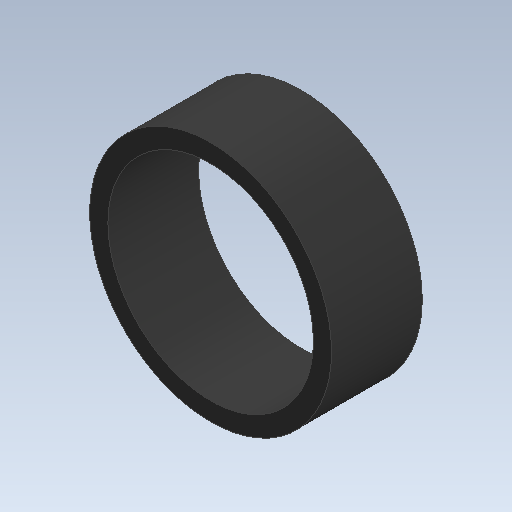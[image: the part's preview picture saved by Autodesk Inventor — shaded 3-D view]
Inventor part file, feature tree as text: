
AUTODESK INVENTOR PART (.ipt)
format: ipt  version: 2020 (Build 240168000, 168)  size: 94,208 bytes
history: native  units: in
note: dims shown in document units (in); Inventor stores cm internally (conversion verified against a paired STEP export)
features: extrude x1, sketch x1
ambient origin geometry x8: Origin, YZ Plane, XZ Plane, XY Plane, X Axis, Y Axis, Z Axis, Center Point
bodies: Solid1 (feature_tree)
feature tree (2):
  extrude  "Extrusion1"  Depth=1.5in
  sketch  "Sketch1"  dims[d0=3.4in d1=4.0in d2=1.5in d3=0.0in]
